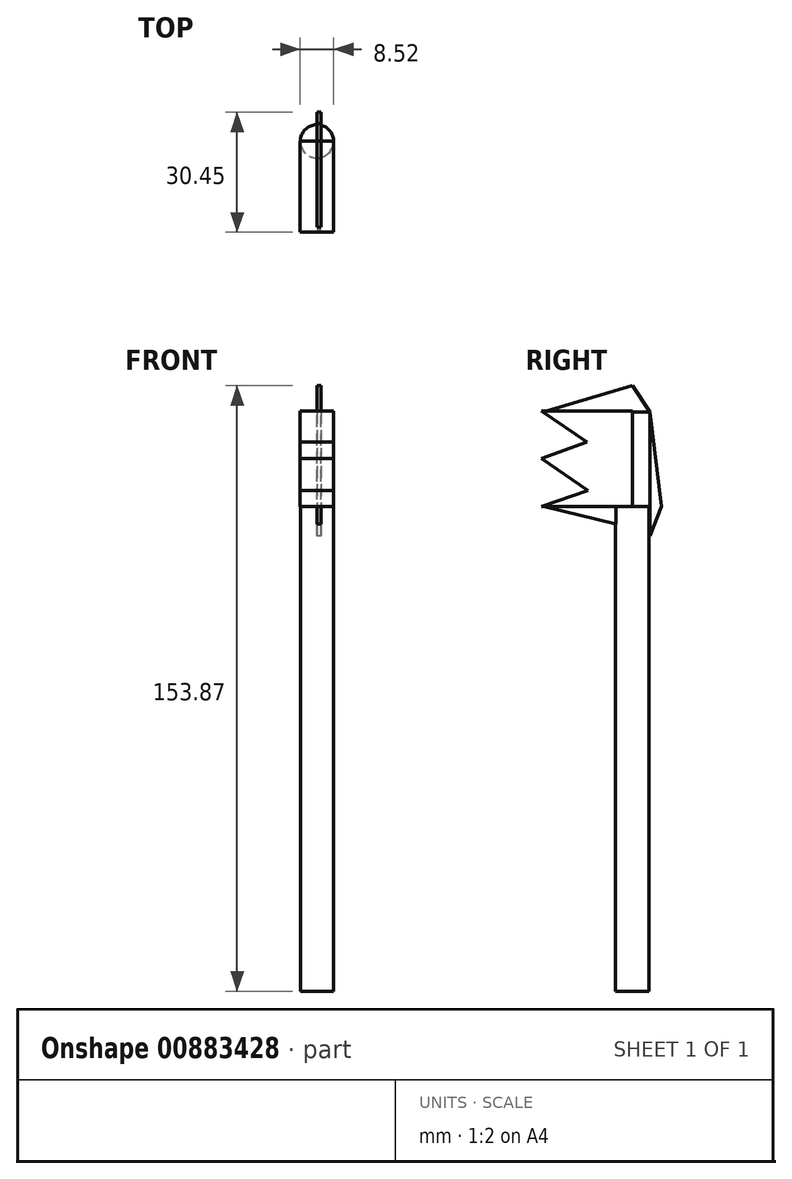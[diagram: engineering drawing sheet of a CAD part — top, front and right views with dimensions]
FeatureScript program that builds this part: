
annotation { "Feature Type Name" : "Feature", "Feature Type Description" : "" }
export const myFeature = defineFeature(function(context is Context, id is Id, definition is map)
    precondition{}
    {
        {
            var Q0;
            Q0=qCreatedBy(makeId("Top.planeOp"),FACE);
            var sketch = newSketch(context, id + "F0", { "sketchPlane" : qUnion([Q0])});
            skArc(sketch, "E0", {"start": v(4.26, 0) * mm, "mid": v(0, 4.26) * mm, "end": v(-4.26, 0) * mm});
            skLineSegment(sketch, "E1.bottom", {"start": v(-4.26, 0) * mm, "end": v(4.26, 0) * mm});
            skLineSegment(sketch, "E1.top", {"start": v(-4.26, 0) * mm, "end": v(4.26, 0) * mm});
            skLineSegment(sketch, "E1.left", {"start": v(-4.26, 0) * mm, "end": v(-4.26, 0) * mm});
            skLineSegment(sketch, "E1.right", {"start": v(4.26, 0) * mm, "end": v(4.26, 0) * mm});
            skLineSegment(sketch, "E2.bottom", {"start": v(4.26, -23.08) * mm, "end": v(-4.26, -23.08) * mm});
            skLineSegment(sketch, "E2.top", {"start": v(4.26, 0) * mm, "end": v(-4.26, 0) * mm});
            skLineSegment(sketch, "E2.left", {"start": v(4.26, -23.08) * mm, "end": v(4.26, 0) * mm});
            skLineSegment(sketch, "E2.right", {"start": v(-4.26, -23.08) * mm, "end": v(-4.26, 0) * mm});
            skSolve(sketch);
        }
        {
            var Q0;
            Q0=makeQuery(id+"F0.imprint","IMPRINT",FACE,{"disambiguationData":[TD([[makeQuery(id+"F0.imprint","IMPRINT",EDGE,{"derivedFrom":sQuery(id+"F0.wireOp",EDGE,"E2.bottom")}),-1.0]])]});
            var Q1;
            {var subQ0=sQuery(id+"F0.wireOp",EDGE,"E2.top");Q1=makeQuery(id+"F0.imprint","IMPRINT",FACE,{"disambiguationData":[TD([[makeQuery(id+"F0.imprint","IMPRINT",EDGE,{"derivedFrom":subQ0}),-1.0]])]});}
            extrude(context, id + "F1", {"entities" : qUnion([Q0, Q1]), "depth" : 24.2 * mm, "offsetDistance" : 25 * mm});
        }
        {
            var Q0;
            Q0=makeQuery(id+"F1.opExtrude","SWEPT_FACE",FACE,{"disambiguationData":[OSD([sQuery(id+"F0.wireOp",EDGE,"E2.left")])]});
            var sketch = newSketch(context, id + "F2", { "sketchPlane" : qUnion([Q0])});
            skLineSegment(sketch, "E3", {"start": v(-23.08, 24.2) * mm, "end": v(-11.54, 16.3) * mm});
            skPoint(sketch, "E3.endSnap0", {"position": v(-11.54, 24.2) * mm});
            skLineSegment(sketch, "E4", {"start": v(-11.54, 16.3) * mm, "end": v(-23.08, 12.1) * mm});
            skLineSegment(sketch, "E5", {"start": v(-23.08, 12.1) * mm, "end": v(-11.27, 4.05) * mm});
            skLineSegment(sketch, "E6", {"start": v(-11.27, 4.05) * mm, "end": v(-23.08, 0) * mm});
            skLineSegment(sketch, "E7", {"start": v(-23.08, 0) * mm, "end": v(-23.08, 12.1) * mm});
            skLineSegment(sketch, "E8", {"start": v(-23.08, 24.83) * mm, "end": v(-23.08, 12.1) * mm});
            skSolve(sketch);
        }
        {
            var Q0;
            {var subQ0=sQuery(id+"F2.wireOp",EDGE,"E3");Q0=makeQuery(id+"F2.imprint","IMPRINT",FACE,{"disambiguationData":[TD([[makeQuery(id+"F2.imprint","IMPRINT",EDGE,{"derivedFrom":subQ0}),-1.0]])]});}
            var Q1;
            Q1=makeQuery(id+"F2.imprint","IMPRINT",FACE,{"disambiguationData":[TD([[makeQuery(id+"F2.imprint","IMPRINT",EDGE,{"derivedFrom":sQuery(id+"F2.wireOp",EDGE,"E5")}),-1.0]])]});
            extrude(context, id + "F3", {"entities" : qUnion([Q0, Q1]), "operationType" : NewBodyOperationType.REMOVE, "oppositeDirection" : true, "depth" : 25 * mm, "offsetDistance" : 25 * mm});
        }
        {
            var Q0;
            Q0=makeQuery(id+"F1.opExtrude","CAP_FACE",FACE,{"disambiguationData":[OSD([sQuery(id+"F0.wireOp",EDGE,"E0"),sQuery(id+"F0.wireOp",EDGE,"E2.bottom"),sQuery(id+"F0.wireOp",EDGE,"E2.left"),sQuery(id+"F0.wireOp",EDGE,"E2.right")])],"isStart":true});
            var sketch = newSketch(context, id + "F4", { "sketchPlane" : qUnion([Q0])});
            skCircle(sketch, "E9", {"center": v(0, 0) * mm, "radius": 4.23 * mm});
            skSolve(sketch);
        }
        {
            var Q0;
            Q0=makeQuery(id+"F4.imprint","IMPRINT",FACE,{"disambiguationData":[TD([[makeQuery(id+"F4.imprint","IMPRINT",EDGE,{"derivedFrom":sQuery(id+"F4.wireOp",EDGE,"E9")}),1.0]])]});
            extrude(context, id + "F5", {"entities" : qUnion([Q0]), "operationType" : NewBodyOperationType.ADD, "depth" : 123.2 * mm, "offsetDistance" : 25 * mm});
        }
        {
            var Q0;
            Q0=qCreatedBy(makeId("Right.planeOp"),FACE);
            var sketch = newSketch(context, id + "F6", { "sketchPlane" : qUnion([Q0])});
            skLineSegment(sketch, "E10", {"start": v(-22.4, 24.03) * mm, "end": v(0, 30.67) * mm});
            skLineSegment(sketch, "E11", {"start": v(0, 30.67) * mm, "end": v(4.48, 24.03) * mm});
            skLineSegment(sketch, "E12", {"start": v(4.48, 24.03) * mm, "end": v(-22.4, 24.03) * mm});
            skLineSegment(sketch, "E13", {"start": v(-22.4, 0) * mm, "end": v(0, -5.46) * mm});
            skLineSegment(sketch, "E14", {"start": v(4.48, 24.03) * mm, "end": v(7.37, 0) * mm});
            skLineSegment(sketch, "E15", {"start": v(7.37, 0) * mm, "end": v(4.48, -7.48) * mm});
            skLineSegment(sketch, "E16", {"start": v(-22.4, 24.03) * mm, "end": v(4.48, 24.03) * mm});
            skLineSegment(sketch, "E17", {"start": v(0, -5.46) * mm, "end": v(0, 0) * mm});
            skLineSegment(sketch, "E18", {"start": v(0, 0) * mm, "end": v(-22.4, 0) * mm});
            skLineSegment(sketch, "E19", {"start": v(4.48, -7.48) * mm, "end": v(4.48, 24.03) * mm});
            skSolve(sketch);
        }
        {
            var Q0;
            Q0=makeQuery(id+"F6.imprint","IMPRINT",FACE,{"disambiguationData":[TD([[makeQuery(id+"F6.imprint","IMPRINT",EDGE,{"derivedFrom":sQuery(id+"F6.wireOp",EDGE,"E10")}),-1.0]])]});
            var Q1;
            Q1=makeQuery(id+"F6.imprint","IMPRINT",FACE,{"disambiguationData":[TD([[makeQuery(id+"F6.imprint","IMPRINT",EDGE,{"derivedFrom":sQuery(id+"F6.wireOp",EDGE,"E13")}),1.0]])]});
            var Q2;
            Q2=makeQuery(id+"F6.imprint","IMPRINT",FACE,{"disambiguationData":[TD([[makeQuery(id+"F6.imprint","IMPRINT",EDGE,{"derivedFrom":sQuery(id+"F6.wireOp",EDGE,"E14")}),-1.0]])]});
            extrude(context, id + "F7", {"entities" : qUnion([Q0, Q1, Q2]), "operationType" : NewBodyOperationType.ADD, "depth" : 1 * mm, "offsetDistance" : 25 * mm});
        }
    });
